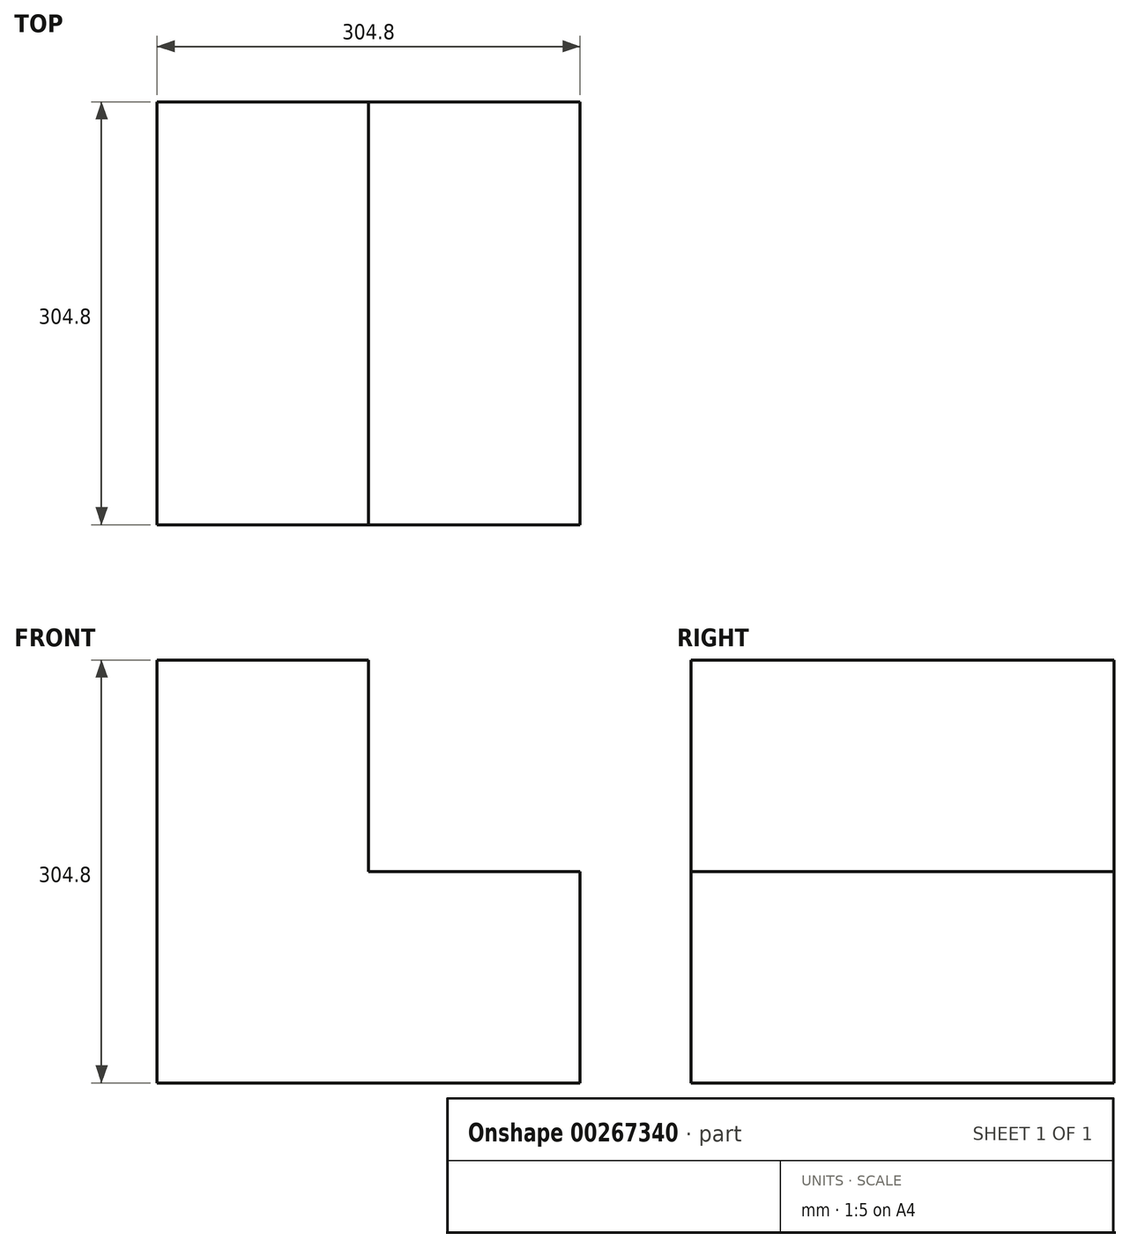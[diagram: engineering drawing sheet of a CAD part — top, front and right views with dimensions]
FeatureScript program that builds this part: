
annotation { "Feature Type Name" : "Feature", "Feature Type Description" : "" }
export const myFeature = defineFeature(function(context is Context, id is Id, definition is map)
    precondition{}
    {
        {
            var Q0;
            Q0=qCreatedBy(makeId("Front.planeOp"),FACE);
            var sketch = newSketch(context, id + "F0", { "sketchPlane" : qUnion([Q0])});
            skLineSegment(sketch, "E0", {"start": v(0, 0) * mm, "end": v(304.8, 0) * mm});
            skLineSegment(sketch, "E1", {"start": v(304.8, 0) * mm, "end": v(304.8, 152.4) * mm});
            skLineSegment(sketch, "E2", {"start": v(304.8, 152.4) * mm, "end": v(152.4, 152.4) * mm});
            skLineSegment(sketch, "E3", {"start": v(152.4, 152.4) * mm, "end": v(152.4, 304.8) * mm});
            skLineSegment(sketch, "E4", {"start": v(152.4, 304.8) * mm, "end": v(0, 304.8) * mm});
            skLineSegment(sketch, "E5", {"start": v(0, 304.8) * mm, "end": v(0, 0) * mm});
            skSolve(sketch);
        }
        {
            var Q0;
            Q0 = qSketchRegion(id + "F0", true);
            extrude(context, id + "F1", {"entities" : qUnion([Q0]), "depth" : 304.8 * mm});
        }
    });
